# Revit family: 1.1.Гибкие вставки WG
name_source: partatom
category: Оборудование
revit_build: Autodesk Revit 2016 (Build: 20151209_0715(x64)
units: mm (PartAtom-declared; Revit-internal decimal feet)

## family parameters
Всегда вертикально = Да
На основе рабочей плоскости = Нет
Общий = Нет
При загрузке вырезать с полостями = Нет
Размер круглого соединителя = Использовать диаметр
Тип детали = Нормальный
Точка расчета площади = Нет

## types (9) — shared parameters
d = 8 мм
Единица измерения = шт.
Завод изготовитель = KORF
Ключевая пометка = Вентиляция
Материал = Резина
Наименование и тех.хар-ка = Гибкая вставка
Раздел = ОВ

## per-type parameters (varying)
| type | А | А1 | А2 | Б | Б1 | Б2 | Высота | Д | Масса единицы | Тип, марка, обозначение | Ширина |
| 50-25 | 540 мм | 520 мм | 500 мм | 290 мм | 270 мм | 250 мм | 250 мм | 172 мм | 3.2 кг | WG 50-25 | 500 мм |
| 50-30 | 540 мм | 520 мм | 500 мм | 340 мм | 320 мм | 300 мм | 300 мм | 172 мм | 3.4 кг | WG 50-30 | 500 мм |
| 40-20 | 440 мм | 420 мм | 400 мм | 240 мм | 220 мм | 200 мм | 200 мм | 172 мм | 2.7 кг | WG 40-20 | 400 мм |
| 60-30 | 640 мм | 620 мм | 600 мм | 340 мм | 320 мм | 300 мм | 300 мм | 172 мм | 3.8 кг | WG 60-30 | 600 мм |
| 60-35 | 640 мм | 620 мм | 600 мм | 390 мм | 370 мм | 350 мм | 350 мм | 172 мм | 4.1 кг | WG 60-35 | 600 мм |
| 70-40 | 740 мм | 720 мм | 700 мм | 440 мм | 420 мм | 400 мм | 400 мм | 172 мм | 4.6 кг | WG 70-40 | 700 мм |
| 80-50 | 840 мм | 820 мм | 800 мм | 540 мм | 520 мм | 500 мм | 500 мм | 172 мм | 5.2 кг | WG 80-50 | 800 мм |
| 90-50 | 960 мм | 930 мм | 900 мм | 560 мм | 530 мм | 500 мм | 500 мм | 175 мм | 6 кг | WG 90-50 | 900 мм |
| 100-50 | 1060 мм | 1030 мм | 1000 мм | 560 мм | 530 мм | 500 мм | 500 мм | 175 мм | 6.4 кг | WG 100-50 | 1000 мм |
